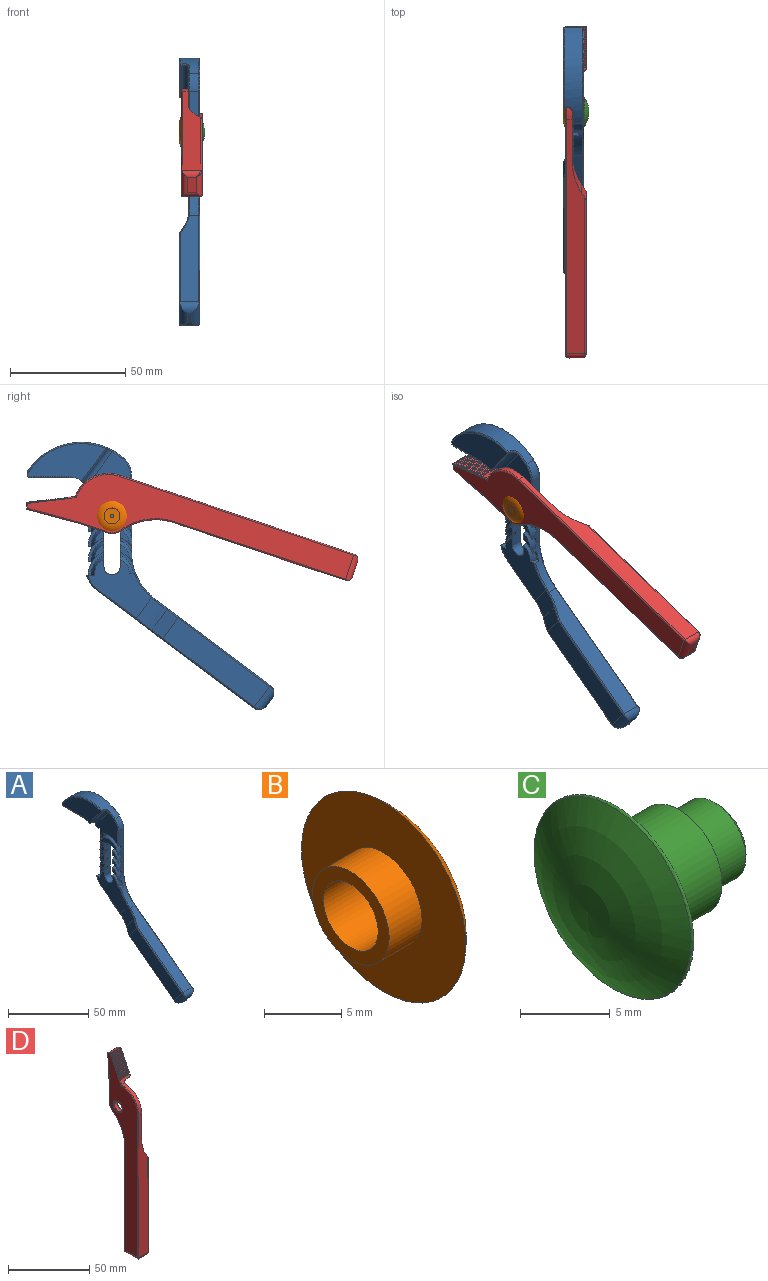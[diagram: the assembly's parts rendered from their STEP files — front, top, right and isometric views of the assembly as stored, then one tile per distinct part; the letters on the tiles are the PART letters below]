
ASSEMBLY  parts=4 mates=3
PART A: 191 faces, bbox 10.7x110.8x119.6 mm
  f0: plane 21.45x19.14mm, normal (-1,0,0), area 239.5mm2, adj f3,f22,f53,f80,f93,f94,f185,f186
  f1: plane 27.52x25.7mm, normal (-1,0,0), area 326mm2, adj f2,f57,f58,f60,f68,f79,f91,f174
  f2: torus R=12.19mm, axis (-1,0,0), area 6.2mm2, adj f1,f65,f79,f175
  f3: cylinder r=10.26mm len=16.08mm, axis (1,0,0), area 46.9mm2, adj f0,f22,f56,f155,f185
  f4: cylinder r=10.26mm len=16.92mm, axis (1,0,0), area 49.4mm2, adj f19,f20,f21,f56,f154,f156,f159,f180
  f5: cylinder r=10.26mm len=4.92mm, axis (1,0,0), area 15mm2, adj f15,f58,f158,f161,f181
  f6: cylinder r=10.26mm len=4.92mm, axis (1,0,0), area 15mm2, adj f12,f58,f162,f172,f182
  f7: cylinder r=10.26mm len=4.92mm, axis (1,0,0), area 15mm2, adj f8,f58,f171,f173,f183
  f8: plane 6.17x4.07mm, normal (-1,0,0), area 10.8mm2, adj f7,f58,f171
  f9: plane 6.17x4.07mm, normal (-1,0,0), area 10.8mm2, adj f60,f170,f179
  f10: plane 0.73x0.59mm, normal (-1,0,0), area 0.2mm2, adj f11,f167,f179
  f11: torus R=25.91mm, axis (-1,0,0), area 1mm2, adj f10,f66,f167,f179
  f12: plane 6.17x4.07mm, normal (-1,0,0), area 10.8mm2, adj f6,f58,f162
  f13: plane 6.17x4.07mm, normal (-1,0,0), area 10.8mm2, adj f60,f163,f168
  f14: plane 0.42x0.36mm, normal (-1,0,0), area 0.1mm2, adj f92,f165,f168
  f15: plane 6.18x4.09mm, normal (-1,0,0), area 10.8mm2, adj f5,f58,f59,f158
  f16: plane 6.18x4.09mm, normal (-1,0,0), area 10.8mm2, adj f59,f60,f157,f166
  f17: plane 0.42x0.36mm, normal (-1,0,0), area 0.1mm2, adj f18,f160,f166
  f18: cylinder r=0.51mm len=1.11mm, axis (0,0,-1), area 0.6mm2, adj f17,f56,f160,f166
  f19: plane 15.14x7.03mm, normal (-1,0,0), area 47mm2, adj f4,f154
  f20: plane 0.42x0.36mm, normal (-1,0,0), area 0.1mm2, adj f4,f21,f156
  f21: cylinder r=0.51mm len=1.11mm, axis (0,0,-1), area 0.6mm2, adj f4,f20,f56,f156
  f22: cylinder r=0.51mm len=11.71mm, axis (0,0,-1), area 9.1mm2, adj f0,f3,f56,f93
  f23: plane 8.49x0.87mm, normal (0,0,-1), area 7.4mm2, adj f24,f25,f64,f152
  f24: plane 33.92x16.26mm, normal (-1,0,0), area 346.9mm2, adj f23,f52,f62,f64,f82,f97,f98,f105
  f25: cylinder r=0.51mm len=1.63mm, axis (0,1,0), area 1mm2, adj f23,f50,f86,f152
  f26: cylinder r=0.51mm len=0.76mm, axis (0,1,0), area 0.3mm2, adj f50,f128,f151
  f27: cylinder r=0.51mm len=0.76mm, axis (0,1,0), area 0.3mm2, adj f50,f106,f149
  f28: cylinder r=0.51mm len=0.76mm, axis (0,1,0), area 0.3mm2, adj f50,f108,f147
  f29: cylinder r=0.51mm len=0.76mm, axis (0,1,0), area 0.3mm2, adj f50,f110,f145
  f30: cylinder r=0.51mm len=0.76mm, axis (0,1,0), area 0.3mm2, adj f50,f112,f143
  f31: cylinder r=0.51mm len=0.76mm, axis (0,1,0), area 0.3mm2, adj f50,f114,f141
  f32: cylinder r=0.51mm len=0.76mm, axis (0,1,0), area 0.3mm2, adj f50,f116,f139
  f33: cylinder r=0.51mm len=0.76mm, axis (0,1,0), area 0.3mm2, adj f50,f118,f137
  f34: cylinder r=0.51mm len=0.76mm, axis (0,1,0), area 0.3mm2, adj f50,f120,f135
  f35: cylinder r=0.51mm len=0.76mm, axis (0,1,0), area 0.3mm2, adj f50,f122,f133
  f36: cylinder r=0.51mm len=0.76mm, axis (0,1,0), area 0.3mm2, adj f50,f124,f131
  f37: cylinder r=0.51mm len=0.76mm, axis (0,1,0), area 0.3mm2, adj f50,f126,f129
  f38: cylinder r=0.51mm len=0.76mm, axis (0,1,0), area 0.3mm2, adj f50,f127,f130
  f39: cylinder r=0.51mm len=0.76mm, axis (0,1,0), area 0.3mm2, adj f50,f125,f132
  f40: cylinder r=0.51mm len=0.76mm, axis (0,1,0), area 0.3mm2, adj f50,f123,f134
  f41: cylinder r=0.51mm len=0.76mm, axis (0,1,0), area 0.3mm2, adj f50,f121,f136
  f42: cylinder r=0.51mm len=0.76mm, axis (0,1,0), area 0.3mm2, adj f50,f119,f138
  f43: cylinder r=0.51mm len=0.76mm, axis (0,1,0), area 0.3mm2, adj f50,f117,f140
  f44: cylinder r=0.51mm len=0.76mm, axis (0,1,0), area 0.3mm2, adj f50,f115,f142
  f45: cylinder r=0.51mm len=0.76mm, axis (0,1,0), area 0.3mm2, adj f50,f113,f144
  f46: cylinder r=0.51mm len=0.76mm, axis (0,1,0), area 0.3mm2, adj f50,f111,f146
  f47: cylinder r=0.51mm len=0.76mm, axis (0,1,0), area 0.3mm2, adj f50,f109,f148
  f48: cylinder r=0.51mm len=0.76mm, axis (0,1,0), area 0.3mm2, adj f50,f107,f150
  f49: cylinder r=0.51mm len=0.76mm, axis (0,1,0), area 0.3mm2, adj f50,f105,f153
  f50: plane 114.22x104.85mm, normal (1,0,0), area 2038.1mm2, adj f25,f26,f27,f28,f29,f30,f31,f32
  f51: plane 13.68x10.26mm, normal (0,-0.8,-0.6), area 16.3mm2, adj f52,f53,f82,f96
  f52: plane 14.11x10.99mm, normal (-0.71,-0.57,-0.42), area 12.6mm2, adj f24,f51,f82,f96,f97
  f53: cylinder r=2.54mm len=16.67mm, axis (0,0.6,-0.8), area 71.9mm2, adj f0,f51,f81,f95
  f54: plane 46.33x38.59mm, normal (-1,0,0), area 545.6mm2, adj f67,f72,f76,f87
  f55: plane 67.87x50.9mm, normal (0,0.6,-0.8), area 557.6mm2, adj f65,f74,f76,f77,f78,f79,f84
  f56: plane 33.25x3.98mm, normal (0,-1,0), area 99.3mm2, adj f3,f4,f18,f21,f22,f66,f70,f92
  f57: cylinder r=3.5mm len=7mm, axis (1,0,0), area 55mm2, adj f1,f50,f58,f60
  f58: plane 22.05x5.05mm, normal (0,-1,0), area 93.8mm2, adj f1,f5,f6,f7,f8,f12,f15,f50
  f59: cylinder r=3.5mm len=7mm, axis (1,0,0), area 34.2mm2, adj f15,f16,f50,f58,f60,f157,f158,f159
  f60: plane 22.07x5.07mm, normal (0,1,0), area 93.8mm2, adj f1,f9,f13,f16,f50,f57,f59,f163
  f61: plane 3.5x2.63mm, normal (0,-0.8,-0.6), area 6mm2, adj f71,f72,f73,f74
  f62: plane 9.06x2.4mm, normal (0,1,0), area 20.9mm2, adj f24,f50,f98,f99,f101,f151
  f63: plane 49.99x37.49mm, normal (0,-0.6,0.8), area 468.5mm2, adj f66,f71,f87,f88,f89,f100
  f64: cylinder r=5.08mm len=8.49mm, axis (-1,0,0), area 50.3mm2, adj f23,f24,f80,f81,f82,f86,f186
  f65: cylinder r=12.7mm len=6.41mm, axis (1,0,0), area 31.8mm2, adj f2,f55,f85,f175
  f66: cylinder r=25.4mm len=20.32mm, axis (-1,0,0), area 79.6mm2, adj f11,f56,f63,f90,f91,f102,f167,f169
  f67: plane 12.33x11.32mm, normal (-0.93,0.3,0.22), area 69.9mm2, adj f54,f68,f77,f88
  f68: cylinder r=22.86mm len=13.92mm, axis (0,-0.6,0.8), area 95.6mm2, adj f1,f67,f78,f89,f90
  f69: cylinder r=27.94mm len=41.38mm, axis (-1,0,0), area 343.8mm2, adj f70,f94,f95,f96,f97,f98,f99,f101
  f70: cylinder r=10.16mm len=7.7mm, axis (-1,0,0), area 34.8mm2, adj f56,f69,f93,f103
  f71: cylinder r=3.81mm len=8.7mm, axis (-1,0,0), area 33.7mm2, adj f61,f63,f72,f73,f87,f100
  f72: cylinder r=3.81mm len=11.36mm, axis (0,-0.6,0.8), area 51.5mm2, adj f54,f61,f71,f75,f87
  f73: cylinder r=3.81mm len=11.36mm, axis (0,0.6,-0.8), area 51.5mm2, adj f50,f61,f71,f83,f100
  f74: cylinder r=3.81mm len=7.98mm, axis (1,0,0), area 33.4mm2, adj f55,f61,f75,f83
  f75: bspline ~5.76x3.81mm, area 2.1mm2, adj f72,f74,f76
  f76: cylinder r=0.51mm len=40.04mm, axis (0,-0.8,-0.6), area 39.6mm2, adj f54,f55,f75,f77
  f77: cylinder r=0.51mm len=4.92mm, axis (-0.37,-0.74,-0.56), area 5mm2, adj f55,f67,f76,f78
  f78: torus R=23.37mm, axis (0,0.6,-0.8), area 7mm2, adj f55,f68,f77,f79
  f79: cylinder r=0.51mm len=16.92mm, axis (0,0.8,0.6), area 16.6mm2, adj f1,f2,f55,f78
  f80: torus R=5.59mm, axis (-1,0,0), area 1mm2, adj f0,f64,f81,f186
  f81: bspline ~3.72x3.57mm, area 3.8mm2, adj f53,f64,f80,f82
  f82: cylinder r=0.51mm len=1.46mm, axis (-1,0,0), area 1mm2, adj f24,f51,f52,f64,f81
  f83: bspline ~5.76x3.81mm, area 2.1mm2, adj f73,f74,f84
  f84: cylinder r=0.51mm len=68.18mm, axis (0,0.8,0.6), area 67.7mm2, adj f50,f55,f83,f85
  f85: torus R=12.19mm, axis (1,0,0), area 6.2mm2, adj f50,f65,f84,f175
  f86: torus R=5.59mm, axis (1,0,0), area 6.6mm2, adj f25,f50,f64,f186
  f87: cylinder r=0.51mm len=40.89mm, axis (0,0.8,0.6), area 40mm2, adj f54,f63,f71,f72,f88
  f88: cylinder r=0.51mm len=5.19mm, axis (-0.37,-0.74,-0.56), area 5mm2, adj f63,f67,f87,f89
  f89: torus R=23.37mm, axis (0,0.6,-0.8), area 5.7mm2, adj f63,f68,f88,f90
  f90: bspline ~6.44x5.27mm, area 1.2mm2, adj f66,f68,f89,f91
  f91: torus R=25.91mm, axis (-1,0,0), area 10.3mm2, adj f1,f66,f90,f178
  f92: cylinder r=0.51mm len=1.11mm, axis (0,0,-1), area 0.6mm2, adj f14,f56,f165,f168
  f93: torus R=9.65mm, axis (-1,0,0), area 6.8mm2, adj f0,f22,f70,f94
  f94: torus R=27.43mm, axis (-1,0,0), area 4.4mm2, adj f0,f69,f93,f95
  f95: bspline ~3.44x3.22mm, area 3.8mm2, adj f53,f69,f94,f96
  f96: cylinder r=0.51mm len=0.96mm, axis (-1,0,0), area 0.8mm2, adj f51,f52,f69,f95,f97
  f97: bspline ~6.32x5.82mm, area 0.5mm2, adj f24,f52,f69,f96,f98
  f98: torus R=27.43mm, axis (1,0,0), area 30.7mm2, adj f24,f62,f69,f97,f99
  f99: cylinder r=0.51mm len=8.55mm, axis (-1,0,0), area 2.5mm2, adj f62,f69,f98,f101
  f100: cylinder r=0.51mm len=51.14mm, axis (0,-0.8,-0.6), area 50.3mm2, adj f50,f63,f71,f73,f102
  f101: torus R=27.43mm, axis (1,0,0), area 37.7mm2, adj f50,f62,f69,f99,f103
  f102: torus R=25.91mm, axis (1,0,0), area 18.9mm2, adj f50,f66,f100,f104
  f103: torus R=9.65mm, axis (1,0,0), area 6.8mm2, adj f50,f70,f101,f104
  f104: cylinder r=0.51mm len=33.25mm, axis (0,0,-1), area 26.5mm2, adj f50,f56,f102,f103
  f105: plane 9.32x1.08mm, normal (0,0.55,-0.83), area 8.1mm2, adj f24,f49,f106,f153
  f106: plane 9x0.51mm, normal (0,-1,0), area 4.5mm2, adj f24,f27,f105,f149
  f107: plane 9.32x1.08mm, normal (0,0.55,-0.83), area 8.1mm2, adj f24,f48,f108,f150
  f108: plane 9x0.51mm, normal (0,-1,0), area 4.5mm2, adj f24,f28,f107,f147
  f109: plane 9.32x1.08mm, normal (0,0.55,-0.83), area 8.1mm2, adj f24,f47,f110,f148
  f110: plane 9x0.51mm, normal (0,-1,0), area 4.5mm2, adj f24,f29,f109,f145
  f111: plane 9.32x1.08mm, normal (0,0.55,-0.83), area 8.1mm2, adj f24,f46,f112,f146
  f112: plane 9x0.51mm, normal (0,-1,0), area 4.5mm2, adj f24,f30,f111,f143
  f113: plane 9.32x1.08mm, normal (0,0.55,-0.83), area 8.1mm2, adj f24,f45,f114,f144
  f114: plane 9x0.51mm, normal (0,-1,0), area 4.5mm2, adj f24,f31,f113,f141
  f115: plane 9.32x1.08mm, normal (0,0.55,-0.83), area 8.1mm2, adj f24,f44,f116,f142
  f116: plane 9x0.51mm, normal (0,-1,0), area 4.5mm2, adj f24,f32,f115,f139
  f117: plane 9.32x1.08mm, normal (0,0.55,-0.83), area 8.1mm2, adj f24,f43,f118,f140
  f118: plane 9x0.51mm, normal (0,-1,0), area 4.5mm2, adj f24,f33,f117,f137
  f119: plane 9.32x1.08mm, normal (0,0.55,-0.83), area 8.1mm2, adj f24,f42,f120,f138
  f120: plane 9x0.51mm, normal (0,-1,0), area 4.5mm2, adj f24,f34,f119,f135
  f121: plane 9.32x1.08mm, normal (0,0.55,-0.83), area 8.1mm2, adj f24,f41,f122,f136
  f122: plane 9x0.51mm, normal (0,-1,0), area 4.5mm2, adj f24,f35,f121,f133
  f123: plane 9.32x1.08mm, normal (0,0.55,-0.83), area 8.1mm2, adj f24,f40,f124,f134
  f124: plane 9x0.51mm, normal (0,-1,0), area 4.5mm2, adj f24,f36,f123,f131
  f125: plane 9.32x1.08mm, normal (0,0.55,-0.83), area 8.1mm2, adj f24,f39,f126,f132
  f126: plane 9x0.51mm, normal (0,-1,0), area 4.5mm2, adj f24,f37,f125,f129
  f127: plane 9.32x1.08mm, normal (0,0.55,-0.83), area 8.1mm2, adj f24,f38,f128,f130
  f128: plane 9x0.51mm, normal (0,-1,0), area 4.5mm2, adj f24,f26,f127,f151
  f129: plane 9.32x1.08mm, normal (0,0.55,-0.83), area 8.1mm2, adj f24,f37,f126,f130
  f130: plane 9x0.51mm, normal (0,-1,0), area 4.5mm2, adj f24,f38,f127,f129
  f131: plane 9.32x1.08mm, normal (0,0.55,-0.83), area 8.1mm2, adj f24,f36,f124,f132
  f132: plane 9x0.51mm, normal (0,-1,0), area 4.5mm2, adj f24,f39,f125,f131
  f133: plane 9.32x1.08mm, normal (0,0.55,-0.83), area 8.1mm2, adj f24,f35,f122,f134
  f134: plane 9x0.51mm, normal (0,-1,0), area 4.5mm2, adj f24,f40,f123,f133
  f135: plane 9.32x1.08mm, normal (0,0.55,-0.83), area 8.1mm2, adj f24,f34,f120,f136
  f136: plane 9x0.51mm, normal (0,-1,0), area 4.5mm2, adj f24,f41,f121,f135
  f137: plane 9.32x1.08mm, normal (0,0.55,-0.83), area 8.1mm2, adj f24,f33,f118,f138
  f138: plane 9x0.51mm, normal (0,-1,0), area 4.5mm2, adj f24,f42,f119,f137
  f139: plane 9.32x1.08mm, normal (0,0.55,-0.83), area 8.1mm2, adj f24,f32,f116,f140
  f140: plane 9x0.51mm, normal (0,-1,0), area 4.5mm2, adj f24,f43,f117,f139
  f141: plane 9.32x1.08mm, normal (0,0.55,-0.83), area 8.1mm2, adj f24,f31,f114,f142
  f142: plane 9x0.51mm, normal (0,-1,0), area 4.5mm2, adj f24,f44,f115,f141
  f143: plane 9.32x1.08mm, normal (0,0.55,-0.83), area 8.1mm2, adj f24,f30,f112,f144
  f144: plane 9x0.51mm, normal (0,-1,0), area 4.5mm2, adj f24,f45,f113,f143
  f145: plane 9.32x1.08mm, normal (0,0.55,-0.83), area 8.1mm2, adj f24,f29,f110,f146
  f146: plane 9x0.51mm, normal (0,-1,0), area 4.5mm2, adj f24,f46,f111,f145
  f147: plane 9.32x1.08mm, normal (0,0.55,-0.83), area 8.1mm2, adj f24,f28,f108,f148
  f148: plane 9x0.51mm, normal (0,-1,0), area 4.5mm2, adj f24,f47,f109,f147
  f149: plane 9.32x1.08mm, normal (0,0.55,-0.83), area 8.1mm2, adj f24,f27,f106,f150
  f150: plane 9x0.51mm, normal (0,-1,0), area 4.5mm2, adj f24,f48,f107,f149
  f151: plane 9.32x1.08mm, normal (0,0.55,-0.83), area 8.1mm2, adj f24,f26,f62,f128
  f152: plane 9.32x1.08mm, normal (0,0.55,-0.83), area 8.1mm2, adj f23,f24,f25,f153
  f153: plane 9x0.51mm, normal (0,-1,0), area 4.5mm2, adj f24,f49,f105,f152
  f154: revolved ~17.95x9.48mm, area 73mm2, adj f4,f19,f56,f155,f156,f180
  f155: plane 18.76x10.76mm, normal (-1,0,0), area 33.1mm2, adj f3,f56,f154,f180,f184
  f156: plane 1.68x0.87mm, normal (0,0,1), area 0.7mm2, adj f4,f20,f21,f56,f154
  f157: revolved ~8.07x6.76mm, area 25.3mm2, adj f16,f56,f59,f159,f160,f166
  f158: revolved ~9.07x6.63mm, area 28.9mm2, adj f5,f15,f59,f159,f181
  f159: plane 18.76x10.76mm, normal (-1,0,0), area 29.8mm2, adj f4,f56,f59,f157,f158,f181,f190
  f160: plane 1.68x0.87mm, normal (0,0,1), area 0.7mm2, adj f17,f18,f56,f157,f166
  f161: plane 10.14x6.76mm, normal (-1,0,0), area 15.3mm2, adj f5,f58,f162,f182,f189
  f162: revolved ~8.78x5.96mm, area 27.7mm2, adj f6,f12,f58,f161,f182
  f163: revolved ~7.78x6.09mm, area 24.3mm2, adj f13,f56,f60,f164,f165,f168
  f164: plane 6.72x5mm, normal (-1,0,0), area 8.7mm2, adj f56,f60,f163,f166
  f165: plane 1.68x0.87mm, normal (0,0,1), area 0.7mm2, adj f14,f56,f92,f163,f168
  f166: cylinder r=10.26mm len=5mm, axis (1,0,0), area 16.3mm2, adj f16,f17,f18,f56,f60,f157,f160,f164
  f167: plane 1.97x1.04mm, normal (0,0,1), area 1mm2, adj f10,f11,f66,f170,f179
  f168: cylinder r=10.26mm len=5mm, axis (1,0,0), area 16.3mm2, adj f13,f14,f56,f60,f92,f163,f165,f169
  f169: plane 6.73x5mm, normal (-1,0,0), area 8.7mm2, adj f56,f60,f66,f168,f170
  f170: revolved ~7.78x6.09mm, area 24.5mm2, adj f9,f60,f66,f167,f169,f179
  f171: revolved ~8.78x5.96mm, area 27.7mm2, adj f7,f8,f58,f172,f183
  f172: plane 10.14x6.76mm, normal (-1,0,0), area 15.3mm2, adj f6,f58,f171,f183,f188
  f173: plane 10.14x6.76mm, normal (-1,0,0), area 15.3mm2, adj f7,f58,f174,f175,f187
  f174: revolved ~8.78x5.96mm, area 28.7mm2, adj f1,f58,f173,f175
  f175: plane 5.07x3.43mm, normal (0,0,1), area 8.3mm2, adj f1,f2,f50,f65,f85,f173,f174,f187
  f176: revolved ~7.78x6.09mm, area 25.7mm2, adj f1,f60,f177,f178
  f177: plane 9.14x6.69mm, normal (-1,0,0), area 12.6mm2, adj f60,f66,f176,f178,f179
  f178: plane 2.69x2.62mm, normal (0,0,1), area 4.8mm2, adj f1,f66,f91,f176,f177
  f179: cylinder r=10.26mm len=5.4mm, axis (1,0,0), area 18.2mm2, adj f9,f10,f11,f60,f66,f167,f170,f177
  f180: plane 3.46x1.82mm, normal (0,0,-1), area 4.8mm2, adj f4,f50,f154,f155,f184,f190
  f181: plane 3.46x1.82mm, normal (0,0,-1), area 4.8mm2, adj f5,f50,f158,f159,f189,f190
  f182: plane 3.46x1.82mm, normal (0,0,-1), area 4.8mm2, adj f6,f50,f161,f162,f188,f189
  f183: plane 3.46x1.82mm, normal (0,0,-1), area 4.8mm2, adj f7,f50,f171,f172,f187,f188
  f184: cylinder r=10.26mm len=7.41mm, axis (-1,0,0), area 19.9mm2, adj f50,f155,f180,f185
  f185: plane 5x4.59mm, normal (0,1,0), area 22.9mm2, adj f0,f3,f50,f184,f186
  f186: plane 5x3.92mm, normal (0,-0.01,-1), area 19.5mm2, adj f0,f50,f64,f80,f86,f185
  f187: cylinder r=10.26mm len=6.35mm, axis (-1,0,0), area 16.5mm2, adj f50,f173,f175,f183
  f188: cylinder r=10.26mm len=6.35mm, axis (-1,0,0), area 16.5mm2, adj f50,f172,f182,f183
  f189: cylinder r=10.26mm len=6.35mm, axis (-1,0,0), area 16.5mm2, adj f50,f161,f181,f182
  f190: cylinder r=10.26mm len=6.35mm, axis (-1,0,0), area 16.5mm2, adj f50,f159,f180,f181
PART B: 7 faces, bbox 5x15x15 mm
  f0: cylinder r=3.5mm len=7mm, axis (1,0,0), area 66mm2, adj f1,f3
  f1: plane 7x7mm, normal (-1,0,0), area 18.8mm2, adj f0,f5
  f2: plane 6.92x6.92mm, normal (1,0,0), area 35.4mm2, adj f4,f6
  f3: plane 15x15mm, normal (-1,0,0), area 138.2mm2, adj f0,f6
  f4: cone r=0mm half-angle=59deg, axis (-1,0,0), area 20.3mm2, adj f2,f5
  f5: cylinder r=2.5mm len=5mm, axis (-1,0,0), area 62.8mm2, adj f1,f4
  f6: torus R=3.46mm, axis (1,0,0), area 165.4mm2, adj f2,f3
PART C: 8 faces, bbox 10.2x13.5x13.5 mm
  f0: sphere r=10.81mm, area 132.2mm2, adj f7
  f1: plane 4.49x4.49mm, normal (1,0,0), area 15.8mm2, adj f6
  f2: cylinder r=2.5mm len=5mm, axis (-1,0,0), area 43.1mm2, adj f3,f6
  f3: plane 6.72x6.72mm, normal (1,0,0), area 15.8mm2, adj f2,f4
  f4: cylinder r=3.36mm len=6.72mm, axis (-1,0,0), area 105.5mm2, adj f3,f5
  f5: cone r=6.5mm half-angle=89.3deg, axis (-1,0,0), area 82.1mm2, adj f4,f7
  f6: cone r=2.5mm half-angle=45deg, axis (-1,0,0), area 5.4mm2, adj f1,f2
  f7: torus R=6.12mm, axis (1,0,0), area 12.5mm2, adj f0,f5
PART D: 114 faces, bbox 9.1x28.1x144.5 mm
  f0: plane 8.49x2.64mm, normal (0,0.43,0.9), area 24.8mm2, adj f27,f28,f61,f113
  f1: plane 8.49x0.03mm, normal (0,-0.9,0.43), area 0.3mm2, adj f28,f62,f69,f112
  f2: plane 8.49x0mm, normal (0,-0.9,0.43), area 0mm2, adj f28,f62,f108,f111
  f3: plane 8.49x0mm, normal (0,-0.9,0.43), area 0mm2, adj f28,f62,f106,f109
  f4: plane 8.49x0mm, normal (0,-0.9,0.43), area 0mm2, adj f28,f62,f104,f107
  f5: plane 8.49x0.01mm, normal (0,-0.9,0.43), area 0.1mm2, adj f28,f62,f102,f105
  f6: plane 8.49x0.01mm, normal (0,-0.9,0.43), area 0.1mm2, adj f28,f62,f100,f103
  f7: plane 8.49x0.01mm, normal (0,-0.9,0.43), area 0.1mm2, adj f28,f62,f98,f101
  f8: plane 8.49x0.01mm, normal (0,-0.9,0.43), area 0.1mm2, adj f28,f62,f96,f99
  f9: plane 8.49x0.01mm, normal (0,-0.9,0.43), area 0.1mm2, adj f28,f62,f94,f97
  f10: plane 8.49x0.01mm, normal (0,-0.9,0.43), area 0.1mm2, adj f28,f62,f92,f95
  f11: plane 8.49x0.01mm, normal (0,-0.9,0.43), area 0.1mm2, adj f28,f62,f90,f93
  f12: plane 8.49x0.02mm, normal (0,-0.9,0.43), area 0.1mm2, adj f28,f62,f88,f91
  f13: plane 8.49x0.02mm, normal (0,-0.9,0.43), area 0.2mm2, adj f28,f62,f86,f89
  f14: plane 8.49x0.02mm, normal (0,-0.9,0.43), area 0.2mm2, adj f28,f62,f84,f87
  f15: plane 8.49x0.02mm, normal (0,-0.9,0.43), area 0.2mm2, adj f28,f62,f82,f85
  f16: plane 8.49x0.02mm, normal (0,-0.9,0.43), area 0.2mm2, adj f28,f62,f80,f83
  f17: plane 8.49x0.02mm, normal (0,-0.9,0.43), area 0.2mm2, adj f28,f62,f78,f81
  f18: plane 8.49x0.02mm, normal (0,-0.9,0.43), area 0.2mm2, adj f28,f62,f76,f79
  f19: plane 8.49x0.02mm, normal (0,-0.9,0.43), area 0.2mm2, adj f28,f62,f74,f77
  f20: plane 8.49x0.03mm, normal (0,-0.9,0.43), area 0.2mm2, adj f28,f62,f72,f75
  f21: plane 8.49x0.03mm, normal (0,-0.9,0.43), area 0.3mm2, adj f28,f62,f70,f73
  f22: plane 8.49x0.03mm, normal (0,-0.9,0.43), area 0.3mm2, adj f28,f62,f68,f71
  f23: plane 8.49x3.04mm, normal (0,-0.9,0.43), area 18.6mm2, adj f24,f28,f33,f35,f38,f41,f66
  f24: cylinder r=0.51mm len=3.55mm, axis (0,-0.43,-0.9), area 2.8mm2, adj f23,f32,f63,f66
  f25: plane 107.22x7.98mm, normal (0,-1,0), area 687.8mm2, adj f34,f36,f37,f38,f46,f54,f64
  f26: plane 12.38x1.98mm, normal (0,1,0), area 24.6mm2, adj f27,f39,f53,f59
  f27: plane 32.29x8.52mm, normal (0,1,-0.06), area 165.1mm2, adj f0,f26,f28,f33,f34,f35,f41,f53
  f28: plane 17.43x10.57mm, normal (1,0,0), area 101.4mm2, adj f0,f1,f2,f3,f4,f5,f6,f7
  f29: plane 78.12x7.98mm, normal (0,1,0), area 605.7mm2, adj f40,f43,f47,f48,f49,f56
  f30: plane 6.92x3.92mm, normal (0,0,-1), area 27.1mm2, adj f43,f44,f45,f46
  f31: plane 70.49x10.98mm, normal (1,0,0), area 774.3mm2, adj f36,f44,f47,f54
  f32: plane 141.22x25.74mm, normal (-1,0,0), area 1726.7mm2, adj f24,f45,f56,f57,f58,f59,f60,f61
  f33: plane 10.13x2.73mm, normal (0,-0.09,-1), area 27.8mm2, adj f23,f27,f35,f41
  f34: plane 34.9x25.64mm, normal (1,0,0), area 682mm2, adj f25,f27,f35,f37,f38,f42,f51,f52
  f35: cylinder r=2mm len=12.94mm, axis (0,-1,0.09), area 33.2mm2, adj f23,f27,f33,f34,f38
  f36: plane 11.49x3.42mm, normal (0.85,0,0.53), area 46.3mm2, adj f25,f31,f37,f48,f54
  f37: cylinder r=25.4mm len=13.46mm, axis (0,-1,0), area 168.2mm2, adj f25,f34,f36,f49,f50
  f38: cylinder r=15.24mm len=15.24mm, axis (-1,0,0), area 58.8mm2, adj f23,f25,f34,f35,f63
  f39: cylinder r=7.62mm len=6.13mm, axis (-1,0,0), area 14.1mm2, adj f26,f40,f52,f58
  f40: cylinder r=25.4mm len=20.43mm, axis (-1,0,0), area 52.2mm2, adj f29,f39,f50,f51,f57
  f41: cylinder r=1.27mm len=10.24mm, axis (0,1,-0.09), area 19.9mm2, adj f23,f27,f28,f33
  f42: cylinder r=3.5mm len=7mm, axis (1,0,0), area 54.8mm2, adj f34,f65
  f43: cylinder r=2.54mm len=8.7mm, axis (-1,0,0), area 28.1mm2, adj f29,f30,f44,f45,f47,f56
  f44: cylinder r=2.54mm len=11.34mm, axis (0,-1,0), area 39mm2, adj f30,f31,f43,f47,f55
  f45: cylinder r=2.54mm len=11.7mm, axis (0,1,0), area 40mm2, adj f30,f32,f43,f46,f56,f64
  f46: cylinder r=2.54mm len=8.34mm, axis (-1,0,0), area 27mm2, adj f25,f30,f45,f55,f64
  f47: cylinder r=0.51mm len=71.35mm, axis (0,0,-1), area 56.5mm2, adj f29,f31,f43,f44,f48
  f48: cylinder r=0.51mm len=3.69mm, axis (0.53,0,-0.85), area 3.2mm2, adj f29,f36,f47,f49
  f49: torus R=25.91mm, axis (0,1,0), area 3.9mm2, adj f29,f37,f48,f50
  f50: bspline ~13.98x3.22mm, area 7.6mm2, adj f37,f40,f49,f51
  f51: torus R=25.91mm, axis (1,0,0), area 11.6mm2, adj f34,f40,f50,f52
  f52: torus R=7.11mm, axis (1,0,0), area 5.5mm2, adj f34,f39,f51,f53
  f53: cylinder r=0.51mm len=12.38mm, axis (0,0,-1), area 7.4mm2, adj f26,f27,f34,f52
  f54: cylinder r=0.51mm len=71.3mm, axis (0,0,1), area 56.5mm2, adj f25,f31,f36,f55
  f55: bspline ~2.64x2.54mm, area 2.2mm2, adj f44,f46,f54
  f56: cylinder r=0.51mm len=78.98mm, axis (0,0,1), area 62.7mm2, adj f29,f32,f43,f45,f57
  f57: torus R=25.91mm, axis (1,0,0), area 19.1mm2, adj f32,f40,f56,f58
  f58: torus R=7.11mm, axis (1,0,0), area 5.5mm2, adj f32,f39,f57,f59
  f59: cylinder r=0.51mm len=12.4mm, axis (0,0,1), area 9.9mm2, adj f26,f32,f58,f60
  f60: cylinder r=0.51mm len=23.6mm, axis (0,0.06,1), area 18.7mm2, adj f27,f32,f59,f61
  f61: cylinder r=0.51mm len=2.86mm, axis (0,-0.9,0.43), area 2.1mm2, adj f0,f32,f60,f62,f113
  f62: cylinder r=0.51mm len=16.4mm, axis (0,-0.43,-0.9), area 5.4mm2, adj f1,f2,f3,f4,f5,f6,f7,f8
  f63: torus R=14.73mm, axis (1,0,0), area 18.7mm2, adj f24,f32,f38,f64
  f64: cylinder r=0.51mm len=108.08mm, axis (0,0,-1), area 85.9mm2, adj f25,f32,f45,f46,f63
  f65: torus R=4.01mm, axis (1,0,0), area 18.5mm2, adj f32,f42
  f66: plane 9x0.46mm, normal (0,0.43,0.9), area 4.5mm2, adj f23,f24,f28,f67
  f67: plane 9x0.91mm, normal (0,-0.99,-0.15), area 8.1mm2, adj f28,f62,f66,f110
  f68: plane 9x0.44mm, normal (0,0.43,0.9), area 4.3mm2, adj f22,f28,f62,f69
  f69: plane 9x0.87mm, normal (0,-0.99,-0.15), area 7.8mm2, adj f1,f28,f62,f68
  f70: plane 9x0.44mm, normal (0,0.43,0.9), area 4.3mm2, adj f21,f28,f62,f71
  f71: plane 9x0.87mm, normal (0,-0.99,-0.15), area 7.8mm2, adj f22,f28,f62,f70
  f72: plane 9x0.44mm, normal (0,0.43,0.9), area 4.3mm2, adj f20,f28,f62,f73
  f73: plane 9x0.87mm, normal (0,-0.99,-0.15), area 7.8mm2, adj f21,f28,f62,f72
  f74: plane 9x0.44mm, normal (0,0.43,0.9), area 4.3mm2, adj f19,f28,f62,f75
  f75: plane 9x0.87mm, normal (0,-0.99,-0.15), area 7.8mm2, adj f20,f28,f62,f74
  f76: plane 9x0.44mm, normal (0,0.43,0.9), area 4.4mm2, adj f18,f28,f62,f77
  f77: plane 9x0.87mm, normal (0,-0.99,-0.15), area 7.9mm2, adj f19,f28,f62,f76
  f78: plane 9x0.44mm, normal (0,0.43,0.9), area 4.4mm2, adj f17,f28,f62,f79
  f79: plane 9x0.88mm, normal (0,-0.99,-0.15), area 7.9mm2, adj f18,f28,f62,f78
  f80: plane 9x0.45mm, normal (0,0.43,0.9), area 4.4mm2, adj f16,f28,f62,f81
  f81: plane 9x0.88mm, normal (0,-0.99,-0.15), area 7.9mm2, adj f17,f28,f62,f80
  f82: plane 9x0.45mm, normal (0,0.43,0.9), area 4.4mm2, adj f15,f28,f62,f83
  f83: plane 9x0.88mm, normal (0,-0.99,-0.15), area 7.9mm2, adj f16,f28,f62,f82
  f84: plane 9x0.45mm, normal (0,0.43,0.9), area 4.4mm2, adj f14,f28,f62,f85
  f85: plane 9x0.88mm, normal (0,-0.99,-0.15), area 7.9mm2, adj f15,f28,f62,f84
  f86: plane 9x0.45mm, normal (0,0.43,0.9), area 4.4mm2, adj f13,f28,f62,f87
  f87: plane 9x0.88mm, normal (0,-0.99,-0.15), area 7.9mm2, adj f14,f28,f62,f86
  f88: plane 9x0.45mm, normal (0,0.43,0.9), area 4.4mm2, adj f12,f28,f62,f89
  f89: plane 9x0.88mm, normal (0,-0.99,-0.15), area 7.9mm2, adj f13,f28,f62,f88
  f90: plane 9x0.45mm, normal (0,0.43,0.9), area 4.4mm2, adj f11,f28,f62,f91
  f91: plane 9x0.89mm, normal (0,-0.99,-0.15), area 8mm2, adj f12,f28,f62,f90
  f92: plane 9x0.45mm, normal (0,0.43,0.9), area 4.4mm2, adj f10,f28,f62,f93
  f93: plane 9x0.89mm, normal (0,-0.99,-0.15), area 8mm2, adj f11,f28,f62,f92
  f94: plane 9x0.45mm, normal (0,0.43,0.9), area 4.4mm2, adj f9,f28,f62,f95
  f95: plane 9x0.89mm, normal (0,-0.99,-0.15), area 8mm2, adj f10,f28,f62,f94
  f96: plane 9x0.45mm, normal (0,0.43,0.9), area 4.4mm2, adj f8,f28,f62,f97
  f97: plane 9x0.89mm, normal (0,-0.99,-0.15), area 8mm2, adj f9,f28,f62,f96
  f98: plane 9x0.45mm, normal (0,0.43,0.9), area 4.5mm2, adj f7,f28,f62,f99
  f99: plane 9x0.89mm, normal (0,-0.99,-0.15), area 8mm2, adj f8,f28,f62,f98
  f100: plane 9x0.45mm, normal (0,0.43,0.9), area 4.5mm2, adj f6,f28,f62,f101
  f101: plane 9x0.9mm, normal (0,-0.99,-0.15), area 8mm2, adj f7,f28,f62,f100
  f102: plane 9x0.45mm, normal (0,0.43,0.9), area 4.5mm2, adj f5,f28,f62,f103
  f103: plane 9x0.9mm, normal (0,-0.99,-0.15), area 8.1mm2, adj f6,f28,f62,f102
  f104: plane 9x0.46mm, normal (0,0.43,0.9), area 4.5mm2, adj f4,f28,f62,f105
  f105: plane 9x0.9mm, normal (0,-0.99,-0.15), area 8.1mm2, adj f5,f28,f62,f104
  f106: plane 9x0.46mm, normal (0,0.43,0.9), area 4.5mm2, adj f3,f28,f62,f107
  f107: plane 9x0.9mm, normal (0,-0.99,-0.15), area 8.1mm2, adj f4,f28,f62,f106
  f108: plane 9x0.46mm, normal (0,0.43,0.9), area 4.5mm2, adj f2,f28,f62,f109
  f109: plane 9x0.9mm, normal (0,-0.99,-0.15), area 8.1mm2, adj f3,f28,f62,f108
  f110: plane 9x0.46mm, normal (0,0.43,0.9), area 4.5mm2, adj f28,f62,f67,f111
  f111: plane 9x0.9mm, normal (0,-0.99,-0.15), area 8.1mm2, adj f2,f28,f62,f110
  f112: plane 9x0.44mm, normal (0,0.43,0.9), area 4.3mm2, adj f1,f28,f62,f113
  f113: plane 9.07x0.8mm, normal (0,-0.99,-0.15), area 6.5mm2, adj f0,f28,f61,f62,f112
PLACE A t=(-12.44,3.27,-10.34)mm fixed
PLACE B rot(axis=(0,-1,0),180deg) t=(-16.44,11.77,18.16)mm
PLACE C rot(axis=(0,0.71,-0.71),180deg) t=(-10.23,11.77,18.16)mm
PLACE D rot(axis=(-1,0,0),71.4deg) t=(-20.44,-95.53,0.84)mm
MATE cylindrical C.f2 <-> D.f39  axis (-1,0,0) through (-17.44,11.77,18.16)mm
MATE cylindrical C.f2 <-> B.f0  axis (-1,0,0) through (-20.44,11.77,18.16)mm
MATE pin_slot A.f3 <-> C.f2  axis (1,0,0) through (-12.44,11.77,18.16)mm
